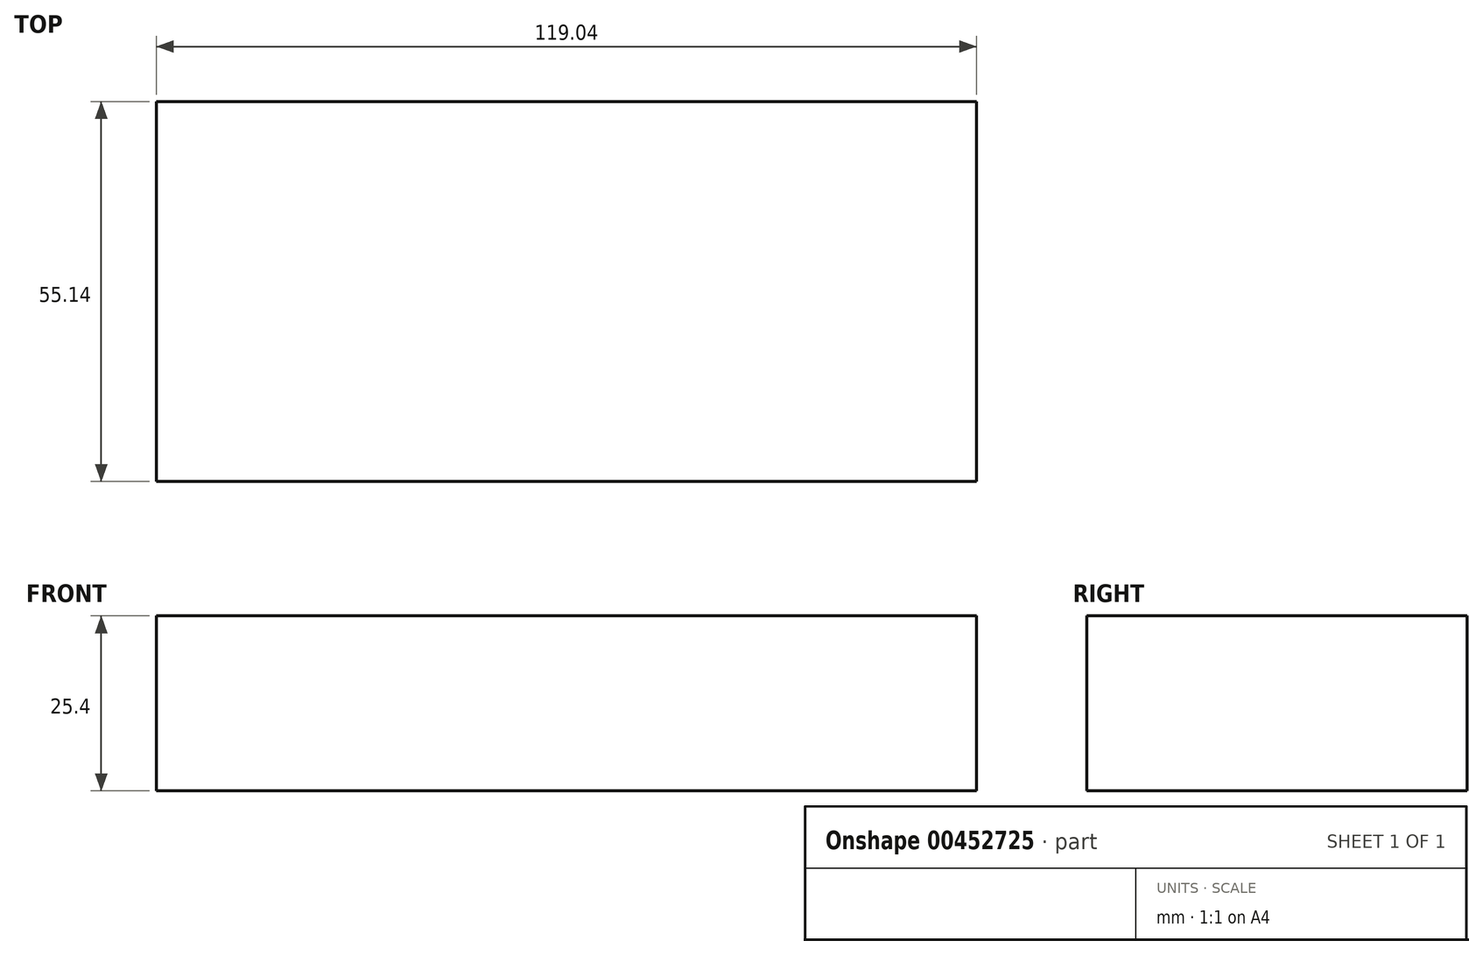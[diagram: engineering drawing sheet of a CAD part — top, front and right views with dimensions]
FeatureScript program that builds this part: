
annotation { "Feature Type Name" : "Feature", "Feature Type Description" : "" }
export const myFeature = defineFeature(function(context is Context, id is Id, definition is map)
    precondition{}
    {
        {
            var Q0;
            Q0=qCreatedBy(makeId("Top.planeOp"),FACE);
            var sketch = newSketch(context, id + "F0", { "sketchPlane" : qUnion([Q0])});
            skLineSegment(sketch, "E0.bottom", {"start": v(0, 0) * mm, "end": v(119.04, 0) * mm});
            skLineSegment(sketch, "E0.top", {"start": v(0, 55.14) * mm, "end": v(119.04, 55.14) * mm});
            skLineSegment(sketch, "E0.left", {"start": v(0, 0) * mm, "end": v(0, 55.14) * mm});
            skLineSegment(sketch, "E0.right", {"start": v(119.04, 0) * mm, "end": v(119.04, 55.14) * mm});
            skSolve(sketch);
        }
        {
            var Q0;
            Q0=makeQuery(id+"F0.imprint","IMPRINT",FACE,{"disambiguationData":[TD([[makeQuery(id+"F0.imprint","IMPRINT",EDGE,{"derivedFrom":sQuery(id+"F0.wireOp",EDGE,"E0.bottom")}),1.0]])]});
            extrude(context, id + "F1", {"entities" : qUnion([Q0]), "depth" : 25.4 * mm});
        }
    });
